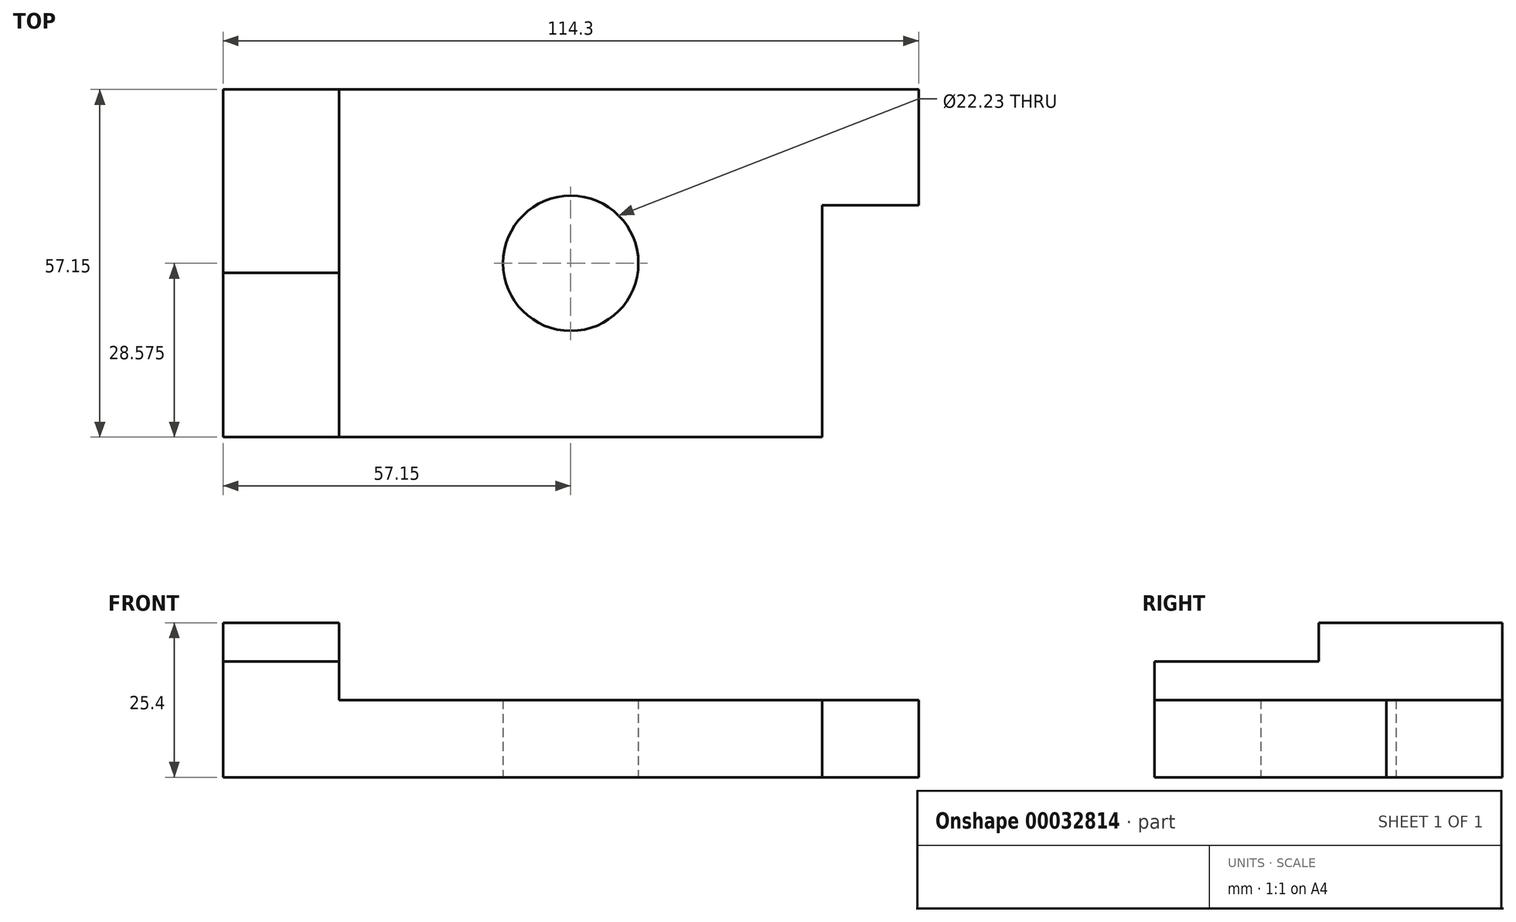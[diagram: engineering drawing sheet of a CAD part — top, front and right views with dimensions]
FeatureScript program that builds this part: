
annotation { "Feature Type Name" : "Feature", "Feature Type Description" : "" }
export const myFeature = defineFeature(function(context is Context, id is Id, definition is map)
    precondition{}
    {
        {
            var Q0;
            Q0=qCreatedBy(makeId("Top.planeOp"),FACE);
            var sketch = newSketch(context, id + "F0", { "sketchPlane" : qUnion([Q0])});
            skLineSegment(sketch, "E0.bottom", {"start": v(-57.15, 19.05) * mm, "end": v(57.15, 19.05) * mm});
            skLineSegment(sketch, "E0.top", {"start": v(-57.15, -38.1) * mm, "end": v(41.28, -38.1) * mm});
            skLineSegment(sketch, "E0.left", {"start": v(-57.15, 19.05) * mm, "end": v(-57.15, -38.1) * mm});
            skLineSegment(sketch, "E0.right", {"start": v(57.15, 19.05) * mm, "end": v(57.15, 0) * mm});
            skLineSegment(sketch, "E1", {"start": v(-57.15, 19.05) * mm, "end": v(-57.15, -11.11) * mm});
            skLineSegment(sketch, "E2", {"start": v(-57.15, -11.11) * mm, "end": v(-38.1, -11.11) * mm});
            skLineSegment(sketch, "E3", {"start": v(-38.1, -11.11) * mm, "end": v(-38.1, 19.05) * mm});
            skLineSegment(sketch, "E4", {"start": v(-38.1, -11.11) * mm, "end": v(-38.1, -38.1) * mm});
            skLineSegment(sketch, "E5", {"start": v(41.28, -38.1) * mm, "end": v(41.28, 0) * mm});
            skLineSegment(sketch, "E6", {"start": v(41.28, 0) * mm, "end": v(57.15, 0) * mm});
            skLineSegment(sketch, "E7", {"start": v(57.15, 19.05) * mm, "end": v(0, 19.05) * mm});
            skCircle(sketch, "E8", {"center": v(0, -9.52) * mm, "radius": 11.11 * mm});
            skPoint(sketch, "E9.orphan", {"position": v(57.15, -38.1) * mm});
            skSolve(sketch);
        }
        {
            var Q0;
            Q0 = qSketchRegion(id + "F0", true);
            extrude(context, id + "F1", {"entities" : qUnion([Q0]), "depth" : 12.7 * mm});
        }
        {
            var Q0;
            Q0=makeQuery(id+"F1.opExtrude","CAP_FACE",FACE,{"disambiguationData":[OSD([sQuery(id+"F0.wireOp",EDGE,"E0.bottom"),sQuery(id+"F0.wireOp",EDGE,"E0.top"),sQuery(id+"F0.wireOp",EDGE,"E0.left"),sQuery(id+"F0.wireOp",EDGE,"E0.right"),sQuery(id+"F0.wireOp",EDGE,"E1"),sQuery(id+"F0.wireOp",EDGE,"E5"),sQuery(id+"F0.wireOp",EDGE,"E6"),sQuery(id+"F0.wireOp",EDGE,"E7"),sQuery(id+"F0.wireOp",EDGE,"E8")])],"isStart":false});
            var sketch = newSketch(context, id + "F2", { "sketchPlane" : qUnion([Q0])});
            skLineSegment(sketch, "E10.0", {"start": v(-38.1, -11.11) * mm, "end": v(-38.1, 19.05) * mm});
            skLineSegment(sketch, "E10.1", {"start": v(-38.1, -11.11) * mm, "end": v(-38.1, -38.1) * mm});
            skLineSegment(sketch, "E11.0", {"start": v(-57.15, -11.11) * mm, "end": v(-38.1, -11.11) * mm});
            skSolve(sketch);
        }
        {
            var Q0;
            {var subQ4=sQuery(id+"F2.wireOp",EDGE,"E10.1");Q0=makeQuery(id+"F2.imprint","IMPRINT",FACE,{"disambiguationData":[TD([[makeQuery(id+"F2.imprint","IMPRINT",EDGE,{"derivedFrom":subQ4}),-1.0]])]});}
            extrude(context, id + "F3", {"entities" : qUnion([Q0]), "operationType" : NewBodyOperationType.ADD, "depth" : 6.35 * mm});
        }
        {
            var Q0;
            {var subQ4=sQuery(id+"F2.wireOp",EDGE,"E10.0");Q0=makeQuery(id+"F2.imprint","IMPRINT",FACE,{"disambiguationData":[TD([[makeQuery(id+"F2.imprint","IMPRINT",EDGE,{"derivedFrom":subQ4}),1.0]])]});}
            extrude(context, id + "F4", {"entities" : qUnion([Q0]), "operationType" : NewBodyOperationType.ADD, "depth" : 12.7 * mm});
        }
    });
